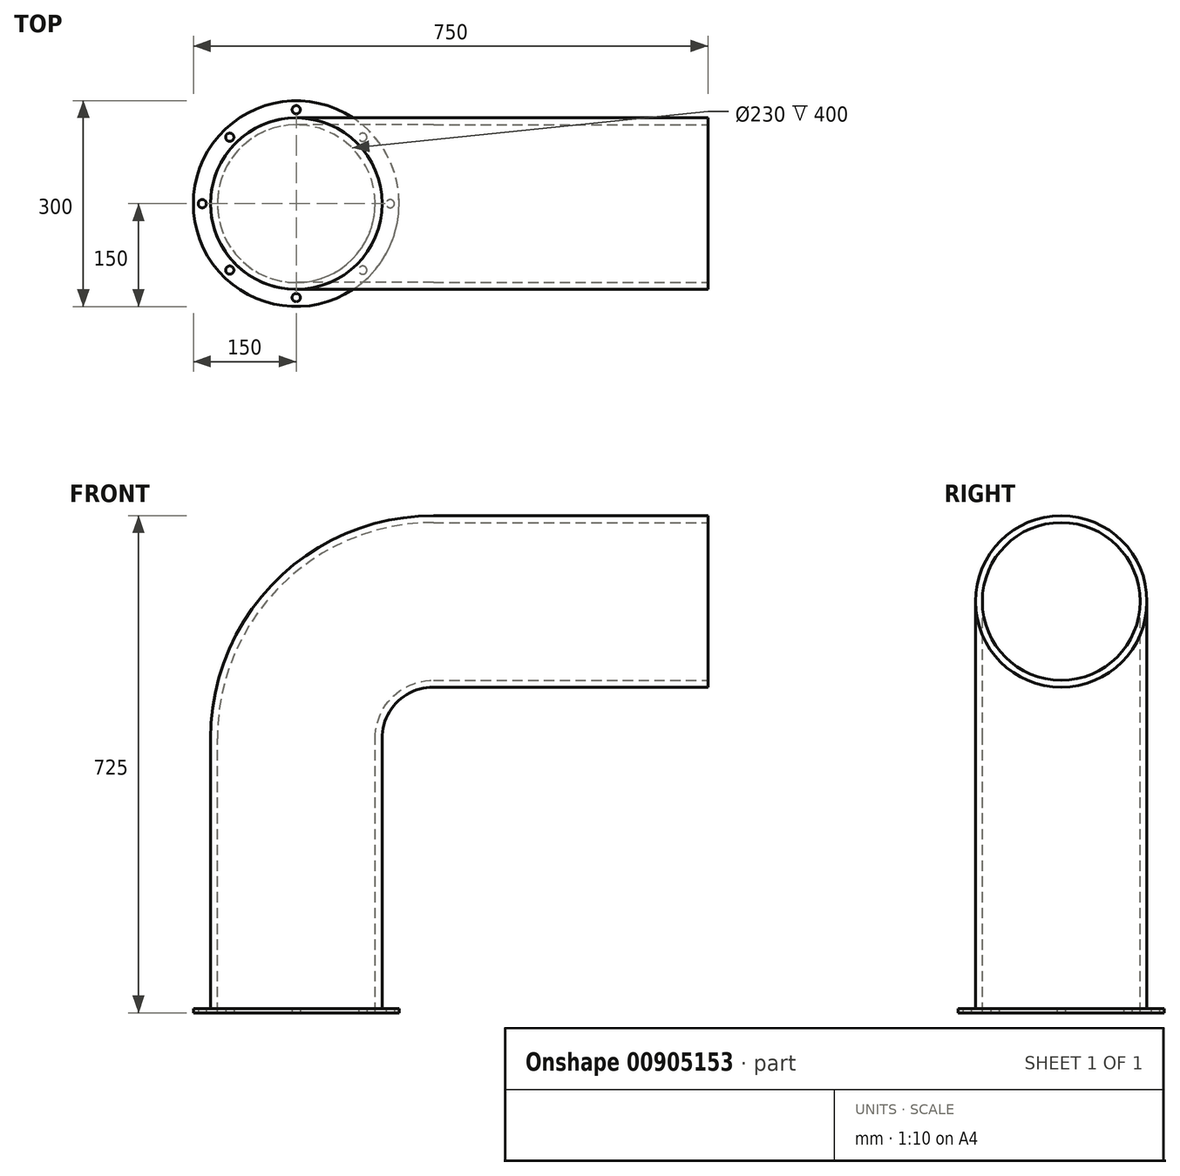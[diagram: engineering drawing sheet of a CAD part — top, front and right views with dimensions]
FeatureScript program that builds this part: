
annotation { "Feature Type Name" : "Feature", "Feature Type Description" : "" }
export const myFeature = defineFeature(function(context is Context, id is Id, definition is map)
    precondition{}
    {
        {
            var Q0;
            Q0=qCreatedBy(makeId("Top.planeOp"),FACE);
            var sketch = newSketch(context, id + "F0", { "sketchPlane" : qUnion([Q0])});
            skCircle(sketch, "E0", {"center": v(0, 0) * mm, "radius": 125 * mm});
            skCircle(sketch, "E1", {"center": v(0, 0) * mm, "radius": 150 * mm});
            skCircle(sketch, "E2", {"center": v(137, 0) * mm, "radius": 6 * mm});
            skCircle(sketch, "E3.1.0", {"center": v(96.87, 96.87) * mm, "radius": 6 * mm});
            skCircle(sketch, "E3.2.0", {"center": v(0, 137) * mm, "radius": 6 * mm});
            skCircle(sketch, "E3.3.0", {"center": v(-96.87, 96.87) * mm, "radius": 6 * mm});
            skCircle(sketch, "E3.4.0", {"center": v(-137, 0) * mm, "radius": 6 * mm});
            skCircle(sketch, "E3.5.0", {"center": v(-96.87, -96.87) * mm, "radius": 6 * mm});
            skCircle(sketch, "E3.6.0", {"center": v(0, -137) * mm, "radius": 6 * mm});
            skCircle(sketch, "E3.7.0", {"center": v(96.87, -96.87) * mm, "radius": 6 * mm});
            skCircle(sketch, "E4", {"center": v(0, 0) * mm, "radius": 115 * mm});
            skSolve(sketch);
        }
        {
            var Q0;
            Q0=makeQuery(id+"F0.imprint","IMPRINT",FACE,{"disambiguationData":[TD([[makeQuery(id+"F0.imprint","IMPRINT",EDGE,{"derivedFrom":sQuery(id+"F0.wireOp",EDGE,"E0")}),-1.0]])]});
            extrude(context, id + "F1", {"entities" : qUnion([Q0]), "depth" : 6 * mm, "offsetDistance" : 25 * mm});
        }
        {
            var Q0;
            Q0=qCreatedBy(makeId("Front.planeOp"),FACE);
            var sketch = newSketch(context, id + "F2", { "sketchPlane" : qUnion([Q0])});
            skLineSegment(sketch, "E5", {"start": v(0, 0) * mm, "end": v(0, 400) * mm});
            skLineSegment(sketch, "E6", {"start": v(200, 600) * mm, "end": v(600, 600) * mm});
            skPoint(sketch, "E7.visualSharp", {"position": v(0, 600) * mm});
            skArc(sketch, "E7.filletArc", {"start": v(200, 600) * mm, "mid": v(58.58, 541.42) * mm, "end": v(0, 400) * mm});
            skSolve(sketch);
        }
        {
            var Q0;
            Q0=qCreatedBy(makeId("Top.planeOp"),FACE);
            var sketch = newSketch(context, id + "F3", { "sketchPlane" : qUnion([Q0])});
            skCircle(sketch, "E8", {"center": v(0, 0) * mm, "radius": 125 * mm});
            skCircle(sketch, "E9", {"center": v(0, 0) * mm, "radius": 115 * mm});
            skSolve(sketch);
        }
        {
            var Q0;
            Q0=makeQuery(id+"F3.imprint","IMPRINT",FACE,{"disambiguationData":[TD([[makeQuery(id+"F3.imprint","IMPRINT",EDGE,{"derivedFrom":sQuery(id+"F3.wireOp",EDGE,"E8")}),1.0]])]});
            var Q1;
            Q1=sQuery(id+"F2.wireOp",EDGE,"E5");
            var Q2;
            Q2=sQuery(id+"F2.wireOp",EDGE,"E6");
            var Q3;
            Q3=sQuery(id+"F2.wireOp",EDGE,"E7.filletArc");
            sweep(context, id + "F4", {"operationType" : NewBodyOperationType.ADD, "profiles" : qUnion([Q0]), "path" : qUnion([Q1, Q2, Q3])});
        }
    });
